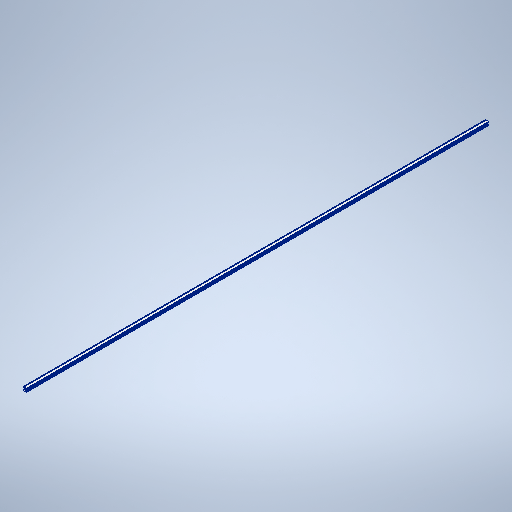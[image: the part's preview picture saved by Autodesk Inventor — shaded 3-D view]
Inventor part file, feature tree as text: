
AUTODESK INVENTOR PART (.ipt)
format: ipt  version: 2025.2 (Build 292293000, 293)  size: 305,664 bytes
history: native  units: mm
features: mirror x2, other x1, extrude x1, sketch x1
ambient origin geometry x8: Origin, YZ Plane, XZ Plane, XY Plane, X Axis, Y Axis, Z Axis, Center Point
bodies: Body1 (feature_tree)
feature tree (5):
  other  "Sólido1"
  extrude  "Extrusão1"  Depth=6.2mm
  mirror  "Espelhar1"
  mirror  "Espelhar2"
  sketch  "Esboço1"  dims[d0=15.0mm d1=6.2mm d2=7.5mm d4=2.0mm d5=6.0mm d7=3.1mm d8=2000.0mm d9=0.0mm d10=0.5mm d11=0.5mm d12=0.2mm d13=0.5mm]
